# Revit family: DCST_Счетчик водяной бытовой_ОСВХ_Нептун
name_source: partatom
category: Арматура трубопроводов
units: mm (PartAtom-declared; Revit-internal decimal feet)

## family parameters
Всегда вертикально = Да
На основе рабочей плоскости = Нет
Общий = Нет
При загрузке вырезать с полостями = Нет
Размер круглого соединителя = Использовать диаметр
Тип детали = Вставляется

## types (2) — shared parameters
ADSK_Единица измерения = шт.
ADSK_Завод-изготовитель = Декаст
ADSK_Количество = 1
LT = ОСВХ_1520
URL = https://www.decast.com
ИПД_ДГ2 = ♦ : импульсный выход (геркон)
ИПД_МИД И = ♦ : импульсный выход (открытый коллектор)
ИПД_МИД Р = ♦ : LoRaWAN
Изготовитель = Декаст

## per-type parameters (varying)
| type | ADSK_Диаметр условный | D | D1 | Dm | F | L1 | L2 | SW | Диаметр условного прохода | Монтажная длина | УГО_Высота | УГО_Длина | УГО_Длина линии |
| ОСВХ-15 | 20 мм | 15.5 мм | 15 мм | 20 мм | 7 мм | 27 мм | 13 мм | 30 мм | 15 мм | 110 мм | 63 мм | 126 мм | 27 мм |
| ОСВХ-20 | 25 мм | 20 мм | 26 мм | 25 мм | 0 мм | 40 мм | 17 мм | 35 мм | 20 мм | 130 мм | 77 мм | 154 мм | 40 мм |
